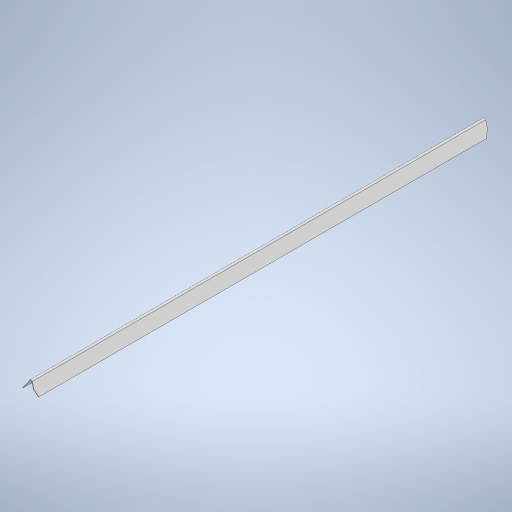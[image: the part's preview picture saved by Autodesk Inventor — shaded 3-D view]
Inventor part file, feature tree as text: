
AUTODESK INVENTOR PART (.ipt)
format: ipt  version: 2023.1 (Build 271208000, 208)  size: 11,607,552 bytes
history: native  units: mm
features: extrude x1, sketch x1
ambient origin geometry x8: Origin, YZ Plane, XZ Plane, XY Plane, X Axis, Y Axis, Z Axis, Center Point
bodies: Solid1 (feature_tree)
feature tree (2):
  extrude  "Extrusion1"  [1 undecoded]
  sketch  "Sketch1"  dims[d0=10.0mm d1=0.0mm]
note: 1 required parameter value undecoded (feature->parameter linkage not recoverable at this tier; creation-order binding heuristic only, values carry confidence <= 0.55)
